# Revit family: MP250160
name_source: partatom
category: Generic Models
units: mm (PartAtom-declared; Revit-internal decimal feet)

## family parameters
Always vertical = No
Can host rebar = No
Cut with Voids When Loaded = No
Part Type = Normal
Room Calculation Point = No
Round Connector Dimension = Use Diameter
Shared = No
Work Plane-Based = Yes

## types (1)
- NBS Standard Parameters
    AssetType = Fixed
    BIMObjectName = Metpro_metprolibrary_channelcablesupports_channelbracket
    Color = Black
    Default Elevation = 1219 mm
    Description = MP250160 - Eco friendly standard foot
    DurationUnit = 1 Year
    Features = SWL 160kg per foot, suitable for both internal & external application (temp between -40 to +80 deg C)
    Finish = Foot - Black / Channel - pre galv
    Keynote = SWL Loading 160kg
    Manufacturer = Metpro ltd
    ManufacturerName = Metpro ltd
    ManufacturerURL = www.metpro.co.uk
    Material = Foot - SBR Recycled Rubber / Channel - Pre galv steel 41x21
    ModelNumber = MP250160
    ModelReference = Channel cable supports
    NBSDescription = Channel cable supports
    NBSReference = 90-55-10/305
    Name = MP250160 - ECO FRIENDLY STANDARD FOOT
    NominalHeight = 95 mm
    NominalLength = 180 mm  [stored 0.590551 ft]
    NominalWidth = 250 mm  [stored 0.82021 ft]
    ProductInformation = www.metpro.co.uk/pdf/MP250160.pdf
    Shape = Rectangular
    Size = 250mm
    URL = www.metpro.co.uk
    Uniclass2 = Pr_65_70_11_19
    Version = 1
    WarrantyDurationUnit = 12 Months
    WarrantyGuarantorParts = 12 Months
    Weight = 2.55

note: [stored X ft] marks values corroborated as IEEE doubles in the binary element streams (Revit-internal decimal feet)

## geometry (parser evidence)
native form markers: Sweep x2
no freeform markers — native parametric forms only
